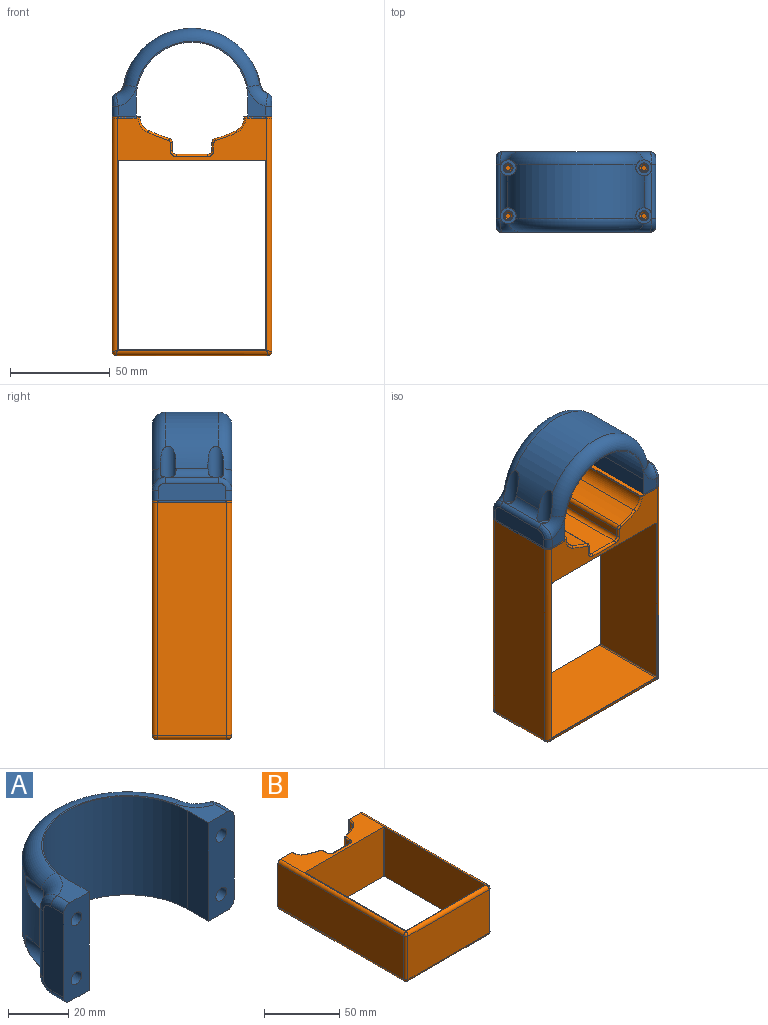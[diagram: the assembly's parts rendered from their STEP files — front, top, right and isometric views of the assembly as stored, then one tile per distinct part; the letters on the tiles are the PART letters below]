
ASSEMBLY  parts=2 mates=1
PART A: 40 faces, bbox 80x47.9x40.1 mm
  f0: cylinder r=35mm len=68.66mm, axis (0,0,-1), area 2363.2mm2, adj f10,f12,f14,f16,f22,f23,f25,f28
  f1: cylinder r=28mm len=56mm, axis (0,0,-1), area 3518.6mm2, adj f2,f7,f8,f9
  f2: plane 40x10mm, normal (-1,0,0), area 400mm2, adj f1,f3,f8,f9
  f3: plane 40x12mm, normal (0,-1,0), area 436.9mm2, adj f2,f4,f8,f9,f18,f19,f35,f39
  f4: plane 34x9.59mm, normal (1,0,0), area 320.5mm2, adj f3,f35,f36,f37,f38,f39
  f5: plane 34x9.59mm, normal (-1,0,0), area 320.5mm2, adj f6,f30,f31,f32,f33,f34
  f6: plane 40x12mm, normal (0,-1,0), area 436.9mm2, adj f5,f7,f8,f9,f20,f21,f30,f34
  f7: plane 40x10mm, normal (1,0,0), area 400mm2, adj f1,f6,f8,f9
  f8: plane 74x38.5mm, normal (0,0,1), area 199.8mm2, adj f1,f2,f3,f6,f7,f24,f25,f26
  f9: plane 74x38.5mm, normal (0,0,-1), area 199.8mm2, adj f1,f2,f3,f6,f7,f27,f28,f29
  f10: cylinder r=4mm len=19.23mm, axis (0,1,0), area 258.7mm2, adj f0,f11,f23,f27,f28
  f11: plane 8x8mm, normal (0,1,0), area 30.6mm2, adj f10,f21
  f12: cylinder r=4mm len=19.23mm, axis (0,1,0), area 258.6mm2, adj f0,f13,f23,f24,f25
  f13: plane 8x8mm, normal (0,1,0), area 30.6mm2, adj f12,f20
  f14: cylinder r=4mm len=19.23mm, axis (0,1,0), area 258.7mm2, adj f0,f15,f22,f25,f26
  f15: plane 8x8mm, normal (0,1,0), area 30.6mm2, adj f14,f19
  f16: cylinder r=4mm len=19.23mm, axis (0,1,0), area 258.6mm2, adj f0,f17,f22,f28,f29
  f17: plane 8x8mm, normal (0,1,0), area 30.6mm2, adj f16,f18
  f18: cylinder r=2.5mm len=8.8mm, axis (0,1,0), area 138.2mm2, adj f3,f17
  f19: cylinder r=2.5mm len=8.8mm, axis (0,1,0), area 138.2mm2, adj f3,f15
  f20: cylinder r=2.5mm len=8.8mm, axis (0,1,0), area 138.2mm2, adj f6,f13
  f21: cylinder r=2.5mm len=8.8mm, axis (0,1,0), area 138.2mm2, adj f6,f11
  f22: cylinder r=6mm len=27mm, axis (0,0,1), area 106.4mm2, adj f0,f14,f16,f26,f29,f37
  f23: cylinder r=6mm len=27mm, axis (0,0,1), area 106.4mm2, adj f0,f10,f12,f24,f27,f32
  f24: torus R=12.5mm, axis (0,0,1), area 78.7mm2, adj f8,f12,f23,f25,f33
  f25: torus R=28.5mm, axis (0,0,1), area 871.3mm2, adj f0,f8,f12,f14,f24,f26
  f26: torus R=12.5mm, axis (0,0,1), area 78.7mm2, adj f8,f14,f22,f25,f38
  f27: torus R=12.5mm, axis (0,0,1), area 78.7mm2, adj f9,f10,f23,f28,f31
  f28: torus R=28.5mm, axis (0,0,1), area 871.3mm2, adj f0,f9,f10,f16,f27,f29
  f29: torus R=12.5mm, axis (0,0,1), area 78.7mm2, adj f9,f16,f22,f28,f36
  f30: cylinder r=3mm len=5.92mm, axis (0,-1,0), area 27.9mm2, adj f5,f6,f9,f31
  f31: bspline ~7.99x7.95mm, area 34mm2, adj f5,f27,f30,f32
  f32: cylinder r=3mm len=27mm, axis (0,0,1), area 97.7mm2, adj f5,f23,f31,f33
  f33: bspline ~7.92x6.85mm, area 34mm2, adj f5,f24,f32,f34
  f34: cylinder r=3mm len=5.92mm, axis (0,1,0), area 27.9mm2, adj f5,f6,f8,f33
  f35: cylinder r=3mm len=5.92mm, axis (0,1,0), area 27.9mm2, adj f3,f4,f9,f36
  f36: bspline ~7.92x6.85mm, area 34mm2, adj f4,f29,f35,f37
  f37: cylinder r=3mm len=27mm, axis (0,0,1), area 97.7mm2, adj f4,f22,f36,f38
  f38: bspline ~7.99x7.95mm, area 34mm2, adj f4,f26,f37,f39
  f39: cylinder r=3mm len=5.92mm, axis (0,-1,0), area 27.9mm2, adj f3,f4,f8,f38
PART B: 78 faces, bbox 80x119.8x40 mm
  f0: plane 93.8x40mm, normal (1,0,0), area 3752mm2, adj f16,f17,f24,f27
  f1: plane 73.1x40mm, normal (0,-1,0), area 2924mm2, adj f16,f17,f24,f25
  f2: plane 93.8x40mm, normal (-1,0,0), area 3752mm2, adj f16,f17,f25,f26
  f3: plane 38x4.04mm, normal (1,0,0), area 153.4mm2, adj f19,f22,f48,f57
  f4: cylinder r=101.57mm len=38mm, axis (0,0,-1), area 428.2mm2, adj f20,f22,f50,f55
  f5: plane 38x0.57mm, normal (1,0,0), area 21.8mm2, adj f6,f20,f52,f53
  f6: plane 40x14mm, normal (0,1,0), area 530.5mm2, adj f5,f7,f16,f17,f30,f35,f52,f53
  f7: plane 117.76x35mm, normal (-1,0,0), area 4121.5mm2, adj f6,f28,f30,f35
  f8: plane 76x35mm, normal (0,-1,0), area 2660mm2, adj f28,f29,f34,f39
  f9: plane 117.76x35mm, normal (1,0,0), area 4121.5mm2, adj f10,f29,f31,f36
  f10: plane 40x14mm, normal (0,1,0), area 530.5mm2, adj f9,f11,f16,f17,f31,f36,f40,f65
  f11: plane 38x0.76mm, normal (-1,0,0), area 28.9mm2, adj f10,f21,f40,f65
  f12: cylinder r=63.81mm len=38mm, axis (0,0,-1), area 430.7mm2, adj f21,f23,f42,f63
  f13: plane 38x3.96mm, normal (-1,0,0), area 150.6mm2, adj f18,f23,f44,f61
  f14: plane 38x16mm, normal (0,1,0), area 608mm2, adj f18,f19,f46,f59
  f15: plane 73.1x40mm, normal (0,1,0), area 2924mm2, adj f16,f17,f26,f27
  f16: plane 117.26x75mm, normal (0,0,1), area 1047.3mm2, adj f0,f1,f2,f6,f10,f15,f24,f25
  f17: plane 117.26x75mm, normal (0,0,-1), area 1047.3mm2, adj f0,f1,f2,f6,f10,f15,f24,f25
  f18: cylinder r=2mm len=38mm, axis (0,0,1), area 119.4mm2, adj f13,f14,f45,f60
  f19: cylinder r=2mm len=38mm, axis (0,0,1), area 119.4mm2, adj f3,f14,f47,f58
  f20: cylinder r=7mm len=38mm, axis (0,0,-1), area 304.8mm2, adj f4,f5,f51,f54
  f21: cylinder r=7mm len=38mm, axis (0,0,-1), area 298mm2, adj f11,f12,f41,f64
  f22: cylinder r=2mm len=38mm, axis (0,0,-1), area 95.5mm2, adj f3,f4,f49,f56
  f23: cylinder r=2mm len=38mm, axis (0,0,-1), area 98.6mm2, adj f12,f13,f43,f62
  f24: cylinder r=0.5mm len=40mm, axis (0,0,-1), area 31.4mm2, adj f0,f1,f16,f17
  f25: cylinder r=0.5mm len=40mm, axis (0,0,1), area 31.4mm2, adj f1,f2,f16,f17
  f26: cylinder r=0.5mm len=40mm, axis (0,0,-1), area 31.4mm2, adj f2,f15,f16,f17
  f27: cylinder r=0.5mm len=40mm, axis (0,0,1), area 31.4mm2, adj f0,f15,f16,f17
  f28: cylinder r=2mm len=35mm, axis (0,0,1), area 110mm2, adj f7,f8,f32,f37
  f29: cylinder r=2mm len=35mm, axis (0,0,-1), area 110mm2, adj f8,f9,f33,f38
  f30: cylinder r=2.5mm len=117.76mm, axis (0,1,0), area 461.7mm2, adj f6,f7,f16,f32
  f31: cylinder r=2.5mm len=117.76mm, axis (0,-1,0), area 461.7mm2, adj f9,f10,f16,f33
  f32: bspline ~3.08x2.5mm, area 8mm2, adj f28,f30,f34
  f33: bspline ~3.08x2.5mm, area 8mm2, adj f29,f31,f34
  f34: cylinder r=2.5mm len=76mm, axis (-1,0,0), area 297mm2, adj f8,f16,f32,f33
  f35: cylinder r=2.5mm len=117.76mm, axis (0,-1,0), area 461.7mm2, adj f6,f7,f17,f37
  f36: cylinder r=2.5mm len=117.76mm, axis (0,1,0), area 461.7mm2, adj f9,f10,f17,f38
  f37: bspline ~3.08x2.5mm, area 8mm2, adj f28,f35,f39
  f38: bspline ~3.08x2.5mm, area 8mm2, adj f29,f36,f39
  f39: cylinder r=2.5mm len=76mm, axis (1,0,0), area 297mm2, adj f8,f17,f37,f38
  f40: cylinder r=1mm len=1mm, axis (0,-1,0), area 1.2mm2, adj f10,f11,f17,f41
  f41: torus R=8mm, axis (0,0,1), area 13mm2, adj f17,f21,f40,f42
  f42: torus R=64.81mm, axis (0,0,1), area 17.9mm2, adj f12,f17,f41,f43
  f43: torus R=1mm, axis (0,0,1), area 3.3mm2, adj f17,f23,f42,f44
  f44: cylinder r=1mm len=3.96mm, axis (0,-1,0), area 6.2mm2, adj f13,f17,f43,f45
  f45: torus R=3mm, axis (0,0,1), area 5.8mm2, adj f17,f18,f44,f46
  f46: cylinder r=1mm len=16mm, axis (-1,0,0), area 25.1mm2, adj f14,f17,f45,f47
  f47: torus R=3mm, axis (0,0,1), area 5.8mm2, adj f17,f19,f46,f48
  f48: cylinder r=1mm len=4.04mm, axis (0,1,0), area 6.3mm2, adj f3,f17,f47,f49
  f49: torus R=1mm, axis (0,0,1), area 3.2mm2, adj f17,f22,f48,f50
  f50: torus R=102.57mm, axis (0,0,1), area 17.8mm2, adj f4,f17,f49,f51
  f51: torus R=8mm, axis (0,0,1), area 13.3mm2, adj f17,f20,f50,f52
  f52: cylinder r=1mm len=1mm, axis (0,1,0), area 0.9mm2, adj f5,f6,f17,f51
  f53: cylinder r=1mm len=1mm, axis (0,-1,0), area 0.9mm2, adj f5,f6,f16,f54
  f54: torus R=8mm, axis (0,0,1), area 13.3mm2, adj f16,f20,f53,f55
  f55: torus R=102.57mm, axis (0,0,1), area 17.8mm2, adj f4,f16,f54,f56
  f56: torus R=1mm, axis (0,0,1), area 3.2mm2, adj f16,f22,f55,f57
  f57: cylinder r=1mm len=4.04mm, axis (0,-1,0), area 6.3mm2, adj f3,f16,f56,f58
  f58: torus R=3mm, axis (0,0,1), area 5.8mm2, adj f16,f19,f57,f59
  f59: cylinder r=1mm len=16mm, axis (1,0,0), area 25.1mm2, adj f14,f16,f58,f60
  f60: torus R=3mm, axis (0,0,1), area 5.8mm2, adj f16,f18,f59,f61
  f61: cylinder r=1mm len=3.96mm, axis (0,1,0), area 6.2mm2, adj f13,f16,f60,f62
  f62: torus R=1mm, axis (0,0,1), area 3.3mm2, adj f16,f23,f61,f63
  f63: torus R=64.81mm, axis (0,0,1), area 17.9mm2, adj f12,f16,f62,f64
  f64: torus R=8mm, axis (0,0,1), area 13mm2, adj f16,f21,f63,f65
  f65: cylinder r=1mm len=1mm, axis (0,1,0), area 1.2mm2, adj f10,f11,f16,f64
  f66: cylinder r=1.25mm len=17.2mm, axis (0,1,0), area 135.1mm2, adj f67,f74
  f67: plane 2.5x2.5mm, normal (0,1,0), area 4.9mm2, adj f66
  f68: cylinder r=1.25mm len=17.2mm, axis (0,1,0), area 135.1mm2, adj f69,f75
  f69: plane 2.5x2.5mm, normal (0,1,0), area 4.9mm2, adj f68
  f70: cylinder r=1.25mm len=17.2mm, axis (0,1,0), area 135.1mm2, adj f71,f76
  f71: plane 2.5x2.5mm, normal (0,1,0), area 4.9mm2, adj f70
  f72: cylinder r=1.25mm len=17.2mm, axis (0,1,0), area 135.1mm2, adj f73,f77
  f73: plane 2.5x2.5mm, normal (0,1,0), area 4.9mm2, adj f72
  f74: cone r=1.25mm half-angle=45deg, axis (0,1,0), area 11.7mm2, adj f10,f66
  f75: cone r=1.25mm half-angle=45deg, axis (0,1,0), area 11.7mm2, adj f10,f68
  f76: cone r=1.25mm half-angle=45deg, axis (0,1,0), area 11.7mm2, adj f6,f70
  f77: cone r=1.25mm half-angle=45deg, axis (0,1,0), area 11.7mm2, adj f6,f72
PLACE A rot(axis=(1,0,0),90deg) t=(11.39,56.86,13.16)mm
PLACE B rot(axis=(1,0,0),90deg) t=(43.27,56.86,-12.83)mm
MATE slider A.f16 <-> B.f74  axis (0,0,-1) through (73.39,48.86,1.16)mm
